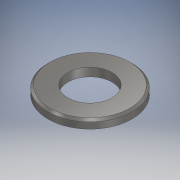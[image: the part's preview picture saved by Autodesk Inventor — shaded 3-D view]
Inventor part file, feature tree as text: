
AUTODESK INVENTOR PART (.ipt)
format: ipt  version: 2019 (Build 230136000, 136)  size: 108,544 bytes
history: native  units: mm
features: extrude x1, chamfer x1, other x1
ambient origin geometry x8: Origin, YZ Plane, XZ Plane, XY Plane, X Axis, Y Axis, Z Axis, Center Point
bodies: Solid1 (feature_tree)
feature tree (3):
  extrude  "Washer"  Depth=10.5mm
  chamfer  "Washer Chamfer"  Distance=20.0mm
  other  "Washer Cross Section"
